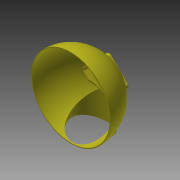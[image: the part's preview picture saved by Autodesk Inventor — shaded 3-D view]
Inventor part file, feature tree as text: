
AUTODESK INVENTOR PART (.ipt)
format: ipt  version: 2015 (Build 190159000, 159)  size: 445,952 bytes
history: native  units: mm
features: extrude x10, sketch x5, other x1, revolve x1, fillet x1
ambient origin geometry x8: Origin, YZ Plane, XZ Plane, XY Plane, X Axis, Y Axis, Z Axis, Center Point
bodies: Body1 (feature_tree)
feature tree (18):
  other  "Sólido1"
  sketch  "Boceto1"  dims[d2=5.0mm d4=2.5mm d6=2.5mm]
  revolve  "Revolución1"  [1 undecoded]
  extrude  "Extrusión1"  Depth=20.0mm
  extrude  "Extrusión2"  Depth=40.0mm TaperAngle=360.0deg
  extrude  "Extrusión3"  Depth=5.0mm
  extrude  "Extrusión4"  Depth=10.0mm
  extrude  "Extrusión5"  Depth=10.0mm
  sketch  "Boceto4"  dims[d11=5.0mm d12=40.0mm d14=360.0deg]
  extrude  "Extrusión7"  Depth=10.0mm
  sketch  "Boceto5"  dims[d16=5.0mm d17=5.0mm]
  extrude  "Extrusión8"  Depth=10.0mm
  extrude  "Extrusión11"  TaperAngle=90.0deg  [1 undecoded]
  extrude  "Extrusión12"  Depth=10.0mm TaperAngle=0.0deg
  fillet  "Empalme2"  Radius=135.0mm
  extrude  "Extrusión13"  Depth=10.0mm TaperAngle=0.0deg
  sketch  "Boceto2"  dims[d8=20.0mm d9=20.0mm]
  sketch  "Boceto9"  dims[d18=5.0mm d19=5.0mm d20=10.0mm d21=280.0mm d22=3.0mm d23=90.0deg d24=1111.0mm d25=0.0mm d26=135.0mm d27=0.0mm d28=130.0mm d29=0.0mm d30=2.451216mm d31=135.0mm d32=0.0mm d33=110.0mm d34=0.0mm d40=100.0mm d41=200.0mm d42=10.0mm d43=0.0mm d45=10.0mm d46=0.0mm d55=4.0mm d56=20.0mm d57=0.0mm d58=20.0mm d59=0.0mm d62=40.0mm d63=280.0mm d64=1111.0mm d65=0.0mm]
note: 2 required parameter values undecoded (feature->parameter linkage not recoverable at this tier; creation-order binding heuristic only, values carry confidence <= 0.55)